# Revit family: Maxlogic beam dedektörü
name_source: partatom
category: Fire Alarm Devices
units: mm (PartAtom-declared; Revit-internal decimal feet)

## family parameters
Cut with Voids When Loaded = No
Host = Face
Maintain Annotation Orientation = Yes
OmniClass Number = 23.85.30.21
OmniClass Title = Environmental Detection/Registration
Part Type = Normal
Room Calculation Point = No
Round Connector Dimension = Use Diameter
Shared = No

## types (6) — shared parameters
Code Performance = EN 54-12 ve EN 54-17
Color = Beyaz
External supply = 24 V/DC
Fax Number = (+)90 216 466 45 10
Main Material = White Plastic PC/ABS
Manufacturer = Mavili Elektronik Ticaret A.Ş.
Model = MaxLogic
Mounting height = Yeksekliğin %10'u kadar tavandan aşağı monte edilir.
Mounting surface = Duvara montaj
Nominal Depth = 109 mm
Nominal Height = 160 mm
Nominal Width = 192 mm
Operating temperature = (-10°C) - (+55°C)
Operatonal Voltage (default) = 20V - 30V DC
Secondary Material = Plastic
URL = https://www.mavili.com.tr
Warranty Duration Labor = 2
Warranty Duration Parts = 2
Warranty Duration Unit = Year
Weight = 830 gr.
zero-valued in all types: Cost, Default Elevation

## per-type parameters (varying)
| type | Description | Device Adress Setup | Installation Manual | Product Code | Public Works Pose Number | Reflector |
| Maxlogic akıllı adresli ışın (beam) tipi duman dedektörü | Akıllı adresli ışın [beam] tipi duman dedektörü | El tipi adresleme cihazı | https://mavilielektronik.com | ML-1170 |  |  |
| Maxlogic akıllı adresli ışın (beam) tipi duman dedektörü, SCI | https://mavilielektronik.com | El tipi adresleme cihazı | www.mavilielektronik.com/ML1170SCI_kk.pdf | ML-1170.SCI |  |  |
| Maxlogic akıllı adresli reflektörlü ışın (beam) tipi duman dedektörü | Akıllı adresli reflektörlü ışın (beam) tipi duman dedektörü | El tipi adresleme cihazı | https://mavilielektronik.com | ML-1173 |  | ML-0171 ve ML-0174 |
| Maxlogic akıllı adresli reflektörlü ışın (beam) tipi duman dedektörü, kısa devre izolatörlü | Adresli reflektörlü ışın (beam) tipi duman dedektörü, kısa devre izolatörlü | El tipi adresleme cihazı | https://mavilielektronik.com | ML-1173.SCI |  | ML-0171 ve ML-0174 |
| Maxlogic konvansiyonel ışın (beam) tipi duman dedektörü | Konvansiyonel ışın [beam] tipi duman dedektörü |  | https://mavilielektronik.com | ML-2170 | 832-111 |  |
| Maxlogic konvansiyonel reflektörlü ışın (beam) tipi duman dedektörü | Konvansiyonel reflektörlü ışın (beam) tipi duman dedektörü |  | https://mavilielektronik.com | ML-2173 |  | ML-0171 ve ML-0174 |

## geometry (parser evidence)
native form markers: Sweep x2
no freeform markers — native parametric forms only
